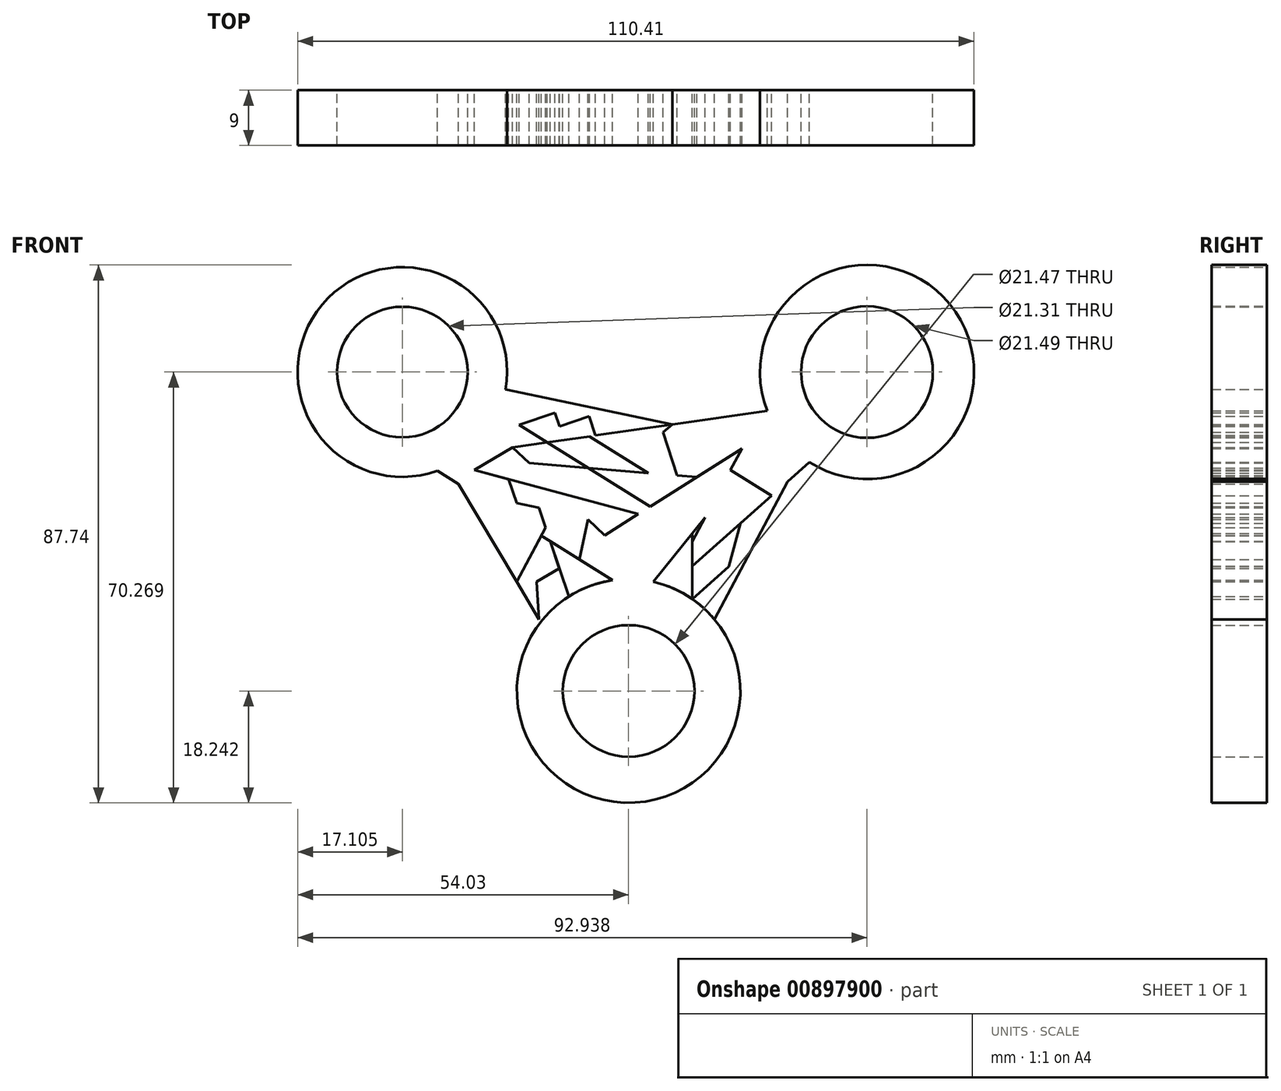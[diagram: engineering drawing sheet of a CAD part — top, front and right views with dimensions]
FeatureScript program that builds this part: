
annotation { "Feature Type Name" : "Feature", "Feature Type Description" : "" }
export const myFeature = defineFeature(function(context is Context, id is Id, definition is map)
    precondition{}
    {
        {
            var Q0;
            Q0=qCreatedBy(makeId("Front.planeOp"),FACE);
            var sketch = newSketch(context, id + "F0", { "sketchPlane" : qUnion([Q0])});
            skCircle(sketch, "E0", {"center": v(-36.93, 11.16) * mm, "radius": 10.65 * mm});
            skCircle(sketch, "E1", {"center": v(-36.93, 11.16) * mm, "radius": 17.1 * mm});
            skCircle(sketch, "E2", {"center": v(38.9, 11.16) * mm, "radius": 10.74 * mm});
            skCircle(sketch, "E3", {"center": v(38.9, 11.16) * mm, "radius": 17.47 * mm});
            skCircle(sketch, "E4", {"center": v(0, -40.87) * mm, "radius": 10.74 * mm});
            skCircle(sketch, "E5", {"center": v(0, -40.87) * mm, "radius": 18.24 * mm});
            skLineSegment(sketch, "E6", {"start": v(-22.38, 2.16) * mm, "end": v(4.03, -23.08) * mm});
            skLineSegment(sketch, "E7", {"start": v(-3.92, -15.48) * mm, "end": v(23.96, 2.11) * mm});
            skLineSegment(sketch, "E8", {"start": v(18.49, -1.34) * mm, "end": v(6.5, -23.82) * mm});
            skLineSegment(sketch, "E9", {"start": v(4.03, -23.08) * mm, "end": v(12.5, -12.58) * mm});
            skLineSegment(sketch, "E10", {"start": v(8.26, -17.83) * mm, "end": v(4.03, -11.12) * mm});
            skLineSegment(sketch, "E11", {"start": v(-1.6, -17.7) * mm, "end": v(8.26, -17.83) * mm});
            skLineSegment(sketch, "E12", {"start": v(10.4, -15.17) * mm, "end": v(6.47, -8.92) * mm});
            skLineSegment(sketch, "E13", {"start": v(1.59, -12) * mm, "end": v(-28.75, -3.86) * mm});
            skLineSegment(sketch, "E14", {"start": v(-15.88, -7.32) * mm, "end": v(-9.76, -25.46) * mm});
            skLineSegment(sketch, "E15", {"start": v(-2.6, -22.81) * mm, "end": v(-31.22, -4.96) * mm});
            skLineSegment(sketch, "E16", {"start": v(-25.05, -8.81) * mm, "end": v(-14.64, -11) * mm});
            skLineSegment(sketch, "E17", {"start": v(-18.23, -10.25) * mm, "end": v(-19.59, -6.32) * mm});
            skLineSegment(sketch, "E18", {"start": v(-16.25, -3.7) * mm, "end": v(11.13, -5.98) * mm});
            skLineSegment(sketch, "E19", {"start": v(4.03, -11.12) * mm, "end": v(-21.14, 4.58) * mm});
            skLineSegment(sketch, "E20", {"start": v(-18.95, -1.12) * mm, "end": v(22.64, 4.8) * mm});
            skLineSegment(sketch, "E21", {"start": v(20.33, -0.18) * mm, "end": v(-20.06, 8.3) * mm});
            skLineSegment(sketch, "E22", {"start": v(-25.18, -4.82) * mm, "end": v(-18.95, -1.12) * mm});
            skLineSegment(sketch, "E23", {"start": v(-27.76, -7.12) * mm, "end": v(-14.64, -29.18) * mm});
            skLineSegment(sketch, "E24", {"start": v(-18.27, -23.08) * mm, "end": v(-13.55, -14.23) * mm});
            skLineSegment(sketch, "E25", {"start": v(10.4, -15.17) * mm, "end": v(10.4, -25.89) * mm});
            skLineSegment(sketch, "E26", {"start": v(10.4, -20.53) * mm, "end": v(29.48, -3.55) * mm});
            skLineSegment(sketch, "E27", {"start": v(16.63, -4.82) * mm, "end": v(23.35, -9.01) * mm});
            skLineSegment(sketch, "E28", {"start": v(-14.64, -29.18) * mm, "end": v(-15.36, -17.62) * mm});
            skLineSegment(sketch, "E29", {"start": v(-15.02, -23.08) * mm, "end": v(-11.3, -20.87) * mm});
            skLineSegment(sketch, "E30", {"start": v(18.28, -13.52) * mm, "end": v(14, -29.18) * mm});
            skLineSegment(sketch, "E31", {"start": v(10.4, -25.89) * mm, "end": v(16.35, -20.6) * mm});
            skLineSegment(sketch, "E32", {"start": v(25.94, -6.7) * mm, "end": v(14, -29.18) * mm});
            skLineSegment(sketch, "E33", {"start": v(19.1, -19.58) * mm, "end": v(18.28, -13.52) * mm});
            skLineSegment(sketch, "E34", {"start": v(-6.4, 0.67) * mm, "end": v(3.2, -5.32) * mm});
            skLineSegment(sketch, "E35", {"start": v(0, -3.32) * mm, "end": v(7.12, 2.6) * mm});
            skLineSegment(sketch, "E36", {"start": v(5.61, 1.34) * mm, "end": v(7.88, -5.71) * mm});
            skLineSegment(sketch, "E37", {"start": v(12.5, 0) * mm, "end": v(12.5, -5.71) * mm});
            skLineSegment(sketch, "E38", {"start": v(-15.28, 0.93) * mm, "end": v(-3.64, 4.86) * mm});
            skLineSegment(sketch, "E39", {"start": v(-6.44, 3.91) * mm, "end": v(-5.35, 0.67) * mm});
            skLineSegment(sketch, "E40", {"start": v(-11.25, 2.29) * mm, "end": v(-12.77, 6.77) * mm});
            skPoint(sketch, "E40.startSnap0", {"position": v(-5.9, 2.29) * mm});
            skLineSegment(sketch, "E41", {"start": v(-12.01, 4.53) * mm, "end": v(-17.88, 2.55) * mm});
            skLineSegment(sketch, "E42", {"start": v(-8.01, -19.44) * mm, "end": v(-6.63, -12.89) * mm});
            skSolve(sketch);
        }
        {
            var Q0;
            Q0=makeQuery(id+"F0.imprint","IMPRINT",FACE,{"disambiguationData":[TD([[makeQuery(id+"F0.imprint","IMPRINT",EDGE,{"derivedFrom":sQuery(id+"F0.wireOp",EDGE,"E0")}),-1.0]])]});
            var Q1;
            {var subQ4=sQuery(id+"F0.wireOp",EDGE,"E15");var subQ6=makeQuery(id+"F0.imprint","INTERSECT",VERTEX,{"derivedFrom":[subQ4,sQuery(id+"F0.wireOp",EDGE,"E16")]});Q1=makeQuery(id+"F0.imprint","IMPRINT",FACE,{"disambiguationData":[TD([[makeQuery(id+"F0.imprint","IMPRINT",EDGE,{"disambiguationData":[TD([[subQ6,1.0]])],"derivedFrom":subQ4}),1.0]])]});}
            var Q2;
            {var subQ0=sQuery(id+"F0.wireOp",EDGE,"E16");var subQ1=sQuery(id+"F0.wireOp",EDGE,"E14");var subQ2=makeQuery(id+"F0.imprint","INTERSECT",VERTEX,{"derivedFrom":[subQ1,subQ0]});Q2=makeQuery(id+"F0.imprint","IMPRINT",FACE,{"disambiguationData":[TD([[makeQuery(id+"F0.imprint","IMPRINT",EDGE,{"disambiguationData":[TD([[subQ2,-1.0]])],"derivedFrom":subQ1}),-1.0]])]});}
            var Q3;
            {var subQ0=sQuery(id+"F0.wireOp",EDGE,"E17");Q3=makeQuery(id+"F0.imprint","IMPRINT",FACE,{"disambiguationData":[TD([[makeQuery(id+"F0.imprint","IMPRINT",EDGE,{"derivedFrom":subQ0}),1.0]])]});}
            var Q4;
            {var subQ5=sQuery(id+"F0.wireOp",EDGE,"E22");Q4=makeQuery(id+"F0.imprint","IMPRINT",FACE,{"disambiguationData":[TD([[makeQuery(id+"F0.imprint","IMPRINT",EDGE,{"derivedFrom":subQ5}),1.0]])]});}
            var Q5;
            {var subQ3=sQuery(id+"F0.wireOp",EDGE,"E6");var subQ4=sQuery(id+"F0.wireOp",EDGE,"E1");var subQ5=makeQuery(id+"F0.imprint","INTERSECT",VERTEX,{"derivedFrom":[subQ4,subQ3]});Q5=makeQuery(id+"F0.imprint","IMPRINT",FACE,{"disambiguationData":[TD([[makeQuery(id+"F0.imprint","IMPRINT",EDGE,{"disambiguationData":[TD([[subQ5,-1.0]])],"derivedFrom":subQ4}),-1.0]])]});}
            var Q6;
            {var subQ3=sQuery(id+"F0.wireOp",EDGE,"E41");Q6=makeQuery(id+"F0.imprint","IMPRINT",FACE,{"disambiguationData":[TD([[makeQuery(id+"F0.imprint","IMPRINT",EDGE,{"derivedFrom":subQ3}),-1.0]])]});}
            var Q7;
            {var subQ1=sQuery(id+"F0.wireOp",EDGE,"E38");var subQ4=sQuery(id+"F0.wireOp",EDGE,"E21");var subQ5=makeQuery(id+"F0.imprint","INTERSECT",VERTEX,{"derivedFrom":[subQ4,subQ1]});Q7=makeQuery(id+"F0.imprint","IMPRINT",FACE,{"disambiguationData":[TD([[makeQuery(id+"F0.imprint","IMPRINT",EDGE,{"disambiguationData":[TD([[subQ5,-1.0]])],"derivedFrom":subQ4}),1.0]])]});}
            var Q8;
            {var subQ0=sQuery(id+"F0.wireOp",EDGE,"E21");var subQ5=sQuery(id+"F0.wireOp",EDGE,"E38");var subQ6=makeQuery(id+"F0.imprint","INTERSECT",VERTEX,{"derivedFrom":[subQ0,subQ5]});Q8=makeQuery(id+"F0.imprint","IMPRINT",FACE,{"disambiguationData":[TD([[makeQuery(id+"F0.imprint","IMPRINT",EDGE,{"disambiguationData":[TD([[subQ6,1.0]])],"derivedFrom":subQ5}),-1.0]])]});}
            var Q9;
            {var subQ4=sQuery(id+"F0.wireOp",EDGE,"E36");Q9=makeQuery(id+"F0.imprint","IMPRINT",FACE,{"disambiguationData":[TD([[makeQuery(id+"F0.imprint","IMPRINT",EDGE,{"derivedFrom":subQ4}),1.0]])]});}
            var Q10;
            {var subQ0=sQuery(id+"F0.wireOp",EDGE,"E7");var subQ1=sQuery(id+"F0.wireOp",EDGE,"E3");var subQ2=makeQuery(id+"F0.imprint","INTERSECT",VERTEX,{"derivedFrom":[subQ1,subQ0]});Q10=makeQuery(id+"F0.imprint","IMPRINT",FACE,{"disambiguationData":[TD([[makeQuery(id+"F0.imprint","IMPRINT",EDGE,{"disambiguationData":[TD([[subQ2,1.0]])],"derivedFrom":subQ1}),-1.0]])]});}
            var Q11;
            {var subQ3=sQuery(id+"F0.wireOp",EDGE,"E27");Q11=makeQuery(id+"F0.imprint","IMPRINT",FACE,{"disambiguationData":[TD([[makeQuery(id+"F0.imprint","IMPRINT",EDGE,{"derivedFrom":subQ3}),1.0]])]});}
            var Q12;
            {var subQ2=sQuery(id+"F0.wireOp",EDGE,"E33");Q12=makeQuery(id+"F0.imprint","IMPRINT",FACE,{"disambiguationData":[TD([[makeQuery(id+"F0.imprint","IMPRINT",EDGE,{"derivedFrom":subQ2}),-1.0]])]});}
            var Q13;
            {var subQ0=sQuery(id+"F0.wireOp",EDGE,"E33");Q13=makeQuery(id+"F0.imprint","IMPRINT",FACE,{"disambiguationData":[TD([[makeQuery(id+"F0.imprint","IMPRINT",EDGE,{"derivedFrom":subQ0}),1.0]])]});}
            var Q14;
            {var subQ0=sQuery(id+"F0.wireOp",EDGE,"E31");Q14=makeQuery(id+"F0.imprint","IMPRINT",FACE,{"disambiguationData":[TD([[makeQuery(id+"F0.imprint","IMPRINT",EDGE,{"derivedFrom":subQ0}),-1.0]])]});}
            var Q15;
            {var subQ0=sQuery(id+"F0.wireOp",EDGE,"E8");var subQ1=sQuery(id+"F0.wireOp",EDGE,"E5");var subQ2=makeQuery(id+"F0.imprint","INTERSECT",VERTEX,{"derivedFrom":[subQ1,subQ0]});Q15=makeQuery(id+"F0.imprint","IMPRINT",FACE,{"disambiguationData":[TD([[makeQuery(id+"F0.imprint","IMPRINT",EDGE,{"disambiguationData":[TD([[subQ2,1.0]])],"derivedFrom":subQ0}),1.0]])]});}
            var Q16;
            {var subQ4=sQuery(id+"F0.wireOp",EDGE,"E5");var subQ6=sQuery(id+"F0.wireOp",EDGE,"E8");var subQ7=makeQuery(id+"F0.imprint","INTERSECT",VERTEX,{"derivedFrom":[subQ4,subQ6]});Q16=makeQuery(id+"F0.imprint","IMPRINT",FACE,{"disambiguationData":[TD([[makeQuery(id+"F0.imprint","IMPRINT",EDGE,{"disambiguationData":[TD([[subQ7,1.0]])],"derivedFrom":subQ6}),-1.0]])]});}
            var Q17;
            {var subQ1=sQuery(id+"F0.wireOp",EDGE,"E5");var subQ4=sQuery(id+"F0.wireOp",EDGE,"E14");var subQ5=makeQuery(id+"F0.imprint","INTERSECT",VERTEX,{"derivedFrom":[subQ1,subQ4]});Q17=makeQuery(id+"F0.imprint","IMPRINT",FACE,{"disambiguationData":[TD([[makeQuery(id+"F0.imprint","IMPRINT",EDGE,{"disambiguationData":[TD([[subQ5,1.0]])],"derivedFrom":subQ1}),-1.0]])]});}
            var Q18;
            Q18=makeQuery(id+"F0.imprint","IMPRINT",FACE,{"disambiguationData":[TD([[makeQuery(id+"F0.imprint","IMPRINT",EDGE,{"derivedFrom":sQuery(id+"F0.wireOp",EDGE,"E2")}),-1.0]])]});
            extrude(context, id + "F1", {"entities" : qUnion([Q0, Q1, Q2, Q3, Q4, Q5, Q6, Q7, Q8, Q9, Q10, Q11, Q12, Q13, Q14, Q15, Q16, Q17, Q18]), "depth" : 9 * mm, "offsetDistance" : 25 * mm});
        }
        {
            var Q0;
            Q0=makeQuery(id+"F0.imprint","IMPRINT",FACE,{"disambiguationData":[TD([[makeQuery(id+"F0.imprint","IMPRINT",EDGE,{"derivedFrom":sQuery(id+"F0.wireOp",EDGE,"E4")}),-1.0]])]});
            var Q1;
            {var subQ0=sQuery(id+"F0.wireOp",EDGE,"E28");var subQ1=sQuery(id+"F0.wireOp",EDGE,"E23");var subQ2=makeQuery(id+"F0.imprint","INTERSECT",VERTEX,{"derivedFrom":[subQ1,subQ0]});Q1=makeQuery(id+"F0.imprint","IMPRINT",FACE,{"disambiguationData":[TD([[makeQuery(id+"F0.imprint","IMPRINT",EDGE,{"disambiguationData":[TD([[subQ2,1.0]])],"derivedFrom":subQ1}),1.0]])]});}
            var Q2;
            {var subQ5=sQuery(id+"F0.wireOp",EDGE,"E29");Q2=makeQuery(id+"F0.imprint","IMPRINT",FACE,{"disambiguationData":[TD([[makeQuery(id+"F0.imprint","IMPRINT",EDGE,{"derivedFrom":subQ5}),1.0]])]});}
            var Q3;
            {var subQ5=sQuery(id+"F0.wireOp",EDGE,"E42");Q3=makeQuery(id+"F0.imprint","IMPRINT",FACE,{"disambiguationData":[TD([[makeQuery(id+"F0.imprint","IMPRINT",EDGE,{"derivedFrom":subQ5}),-1.0]])]});}
            var Q4;
            {var subQ3=sQuery(id+"F0.wireOp",EDGE,"E11");Q4=makeQuery(id+"F0.imprint","IMPRINT",FACE,{"disambiguationData":[TD([[makeQuery(id+"F0.imprint","IMPRINT",EDGE,{"derivedFrom":subQ3}),-1.0]])]});}
            var Q5;
            {var subQ7=sQuery(id+"F0.wireOp",EDGE,"E27");Q5=makeQuery(id+"F0.imprint","IMPRINT",FACE,{"disambiguationData":[TD([[makeQuery(id+"F0.imprint","IMPRINT",EDGE,{"derivedFrom":subQ7}),-1.0]])]});}
            var Q6;
            {var subQ0=sQuery(id+"F0.wireOp",EDGE,"E18");var subQ1=sQuery(id+"F0.wireOp",EDGE,"E6");var subQ2=makeQuery(id+"F0.imprint","INTERSECT",VERTEX,{"derivedFrom":[subQ1,subQ0]});Q6=makeQuery(id+"F0.imprint","IMPRINT",FACE,{"disambiguationData":[TD([[makeQuery(id+"F0.imprint","IMPRINT",EDGE,{"disambiguationData":[TD([[subQ2,-1.0]])],"derivedFrom":subQ1}),1.0]])]});}
            var Q7;
            {var subQ0=sQuery(id+"F0.wireOp",EDGE,"E34");var subQ6=sQuery(id+"F0.wireOp",EDGE,"E18");var subQ8=makeQuery(id+"F0.imprint","INTERSECT",VERTEX,{"derivedFrom":[subQ6,subQ0]});Q7=makeQuery(id+"F0.imprint","IMPRINT",FACE,{"disambiguationData":[TD([[makeQuery(id+"F0.imprint","IMPRINT",EDGE,{"disambiguationData":[TD([[subQ8,1.0]])],"derivedFrom":subQ6}),1.0]])]});}
            var Q8;
            {var subQ6=sQuery(id+"F0.wireOp",EDGE,"E12");Q8=makeQuery(id+"F0.imprint","IMPRINT",FACE,{"disambiguationData":[TD([[makeQuery(id+"F0.imprint","IMPRINT",EDGE,{"derivedFrom":subQ6}),-1.0]])]});}
            var Q9;
            {var subQ0=sQuery(id+"F0.wireOp",EDGE,"E10");Q9=makeQuery(id+"F0.imprint","IMPRINT",FACE,{"disambiguationData":[TD([[makeQuery(id+"F0.imprint","IMPRINT",EDGE,{"derivedFrom":subQ0}),-1.0]])]});}
            var Q10;
            {var subQ4=sQuery(id+"F0.wireOp",EDGE,"E10");Q10=makeQuery(id+"F0.imprint","IMPRINT",FACE,{"disambiguationData":[TD([[makeQuery(id+"F0.imprint","IMPRINT",EDGE,{"derivedFrom":subQ4}),1.0]])]});}
            var Q11;
            {var subQ6=sQuery(id+"F0.wireOp",EDGE,"E22");Q11=makeQuery(id+"F0.imprint","IMPRINT",FACE,{"disambiguationData":[TD([[makeQuery(id+"F0.imprint","IMPRINT",EDGE,{"derivedFrom":subQ6}),-1.0]])]});}
            extrude(context, id + "F2", {"entities" : qUnion([Q0, Q1, Q2, Q3, Q4, Q5, Q6, Q7, Q8, Q9, Q10, Q11]), "depth" : 9 * mm, "offsetDistance" : 25 * mm});
        }
    });
